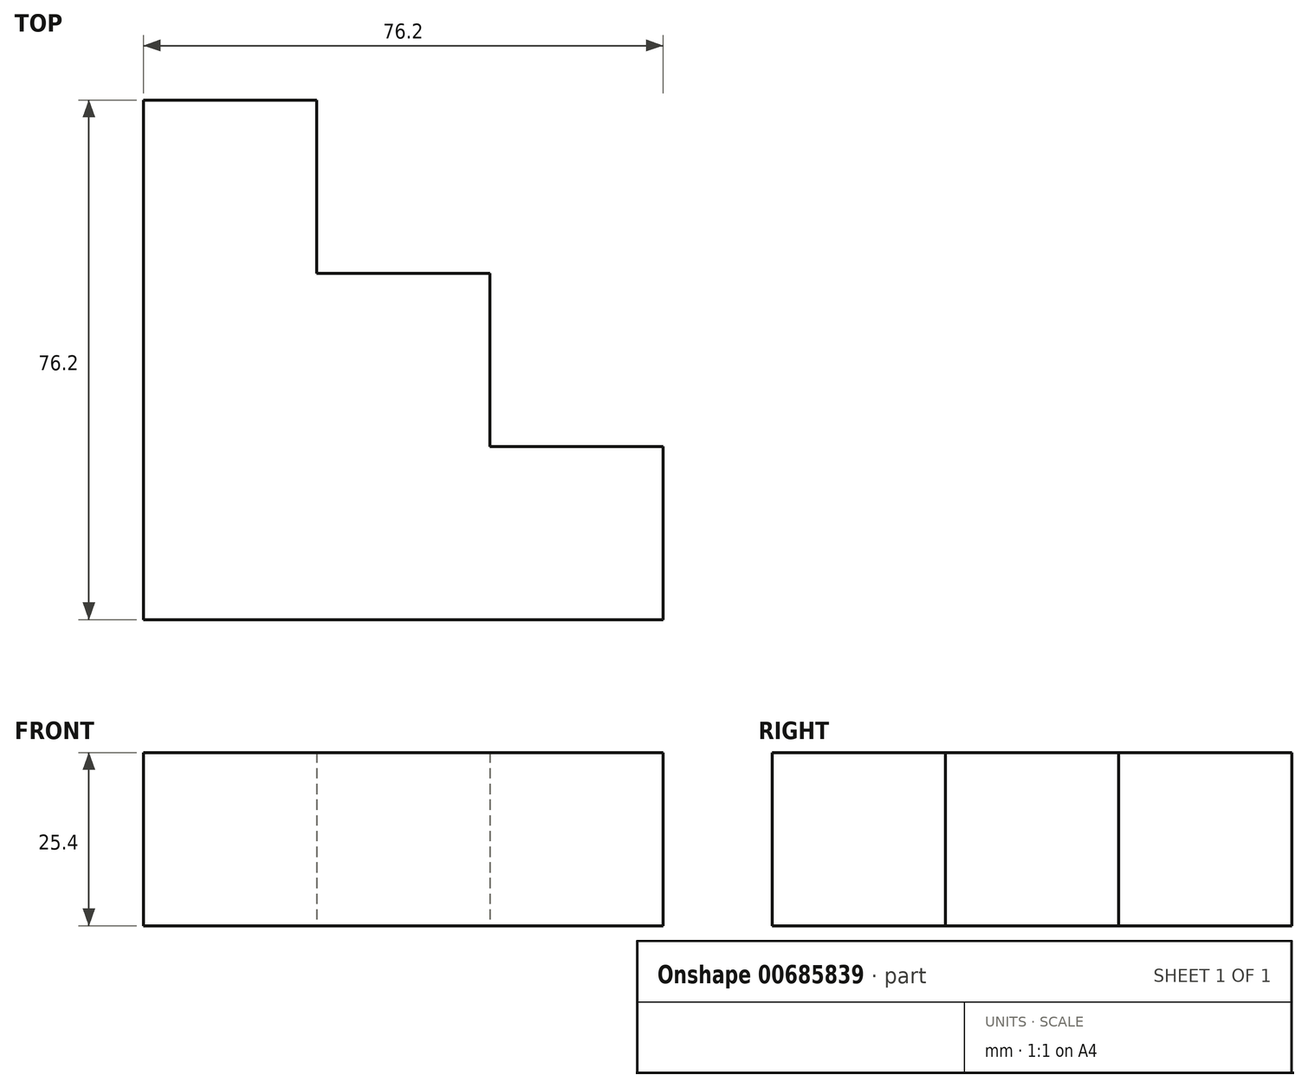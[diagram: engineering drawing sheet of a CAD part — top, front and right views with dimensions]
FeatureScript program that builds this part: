
annotation { "Feature Type Name" : "Feature", "Feature Type Description" : "" }
export const myFeature = defineFeature(function(context is Context, id is Id, definition is map)
    precondition{}
    {
        {
            var Q0;
            Q0=qCreatedBy(makeId("Top.planeOp"),FACE);
            var sketch = newSketch(context, id + "F0", { "sketchPlane" : qUnion([Q0])});
            skLineSegment(sketch, "E0.bottom", {"start": v(-62.6, 66.32) * mm, "end": v(-37.2, 66.32) * mm});
            skLineSegment(sketch, "E0.top", {"start": v(-62.6, -9.88) * mm, "end": v(13.6, -9.88) * mm});
            skLineSegment(sketch, "E0.left", {"start": v(-62.6, 66.32) * mm, "end": v(-62.6, -9.88) * mm});
            skLineSegment(sketch, "E1.bottom", {"start": v(-11.8, 40.92) * mm, "end": v(-37.2, 40.92) * mm});
            skLineSegment(sketch, "E1.right", {"start": v(-37.2, 40.92) * mm, "end": v(-37.2, 66.32) * mm});
            skLineSegment(sketch, "E2.top", {"start": v(-11.8, 15.52) * mm, "end": v(13.6, 15.52) * mm});
            skLineSegment(sketch, "E2.left", {"start": v(-11.8, 40.92) * mm, "end": v(-11.8, 15.52) * mm});
            skLineSegment(sketch, "E3.trimOffspring", {"start": v(13.6, 15.52) * mm, "end": v(13.6, -9.88) * mm});
            skSolve(sketch);
        }
        {
            var Q0;
            Q0 = qSketchRegion(id + "F0", true);
            extrude(context, id + "F1", {"entities" : qUnion([Q0]), "depth" : 25.4 * mm, "offsetDistance" : 25.4 * mm});
        }
    });
